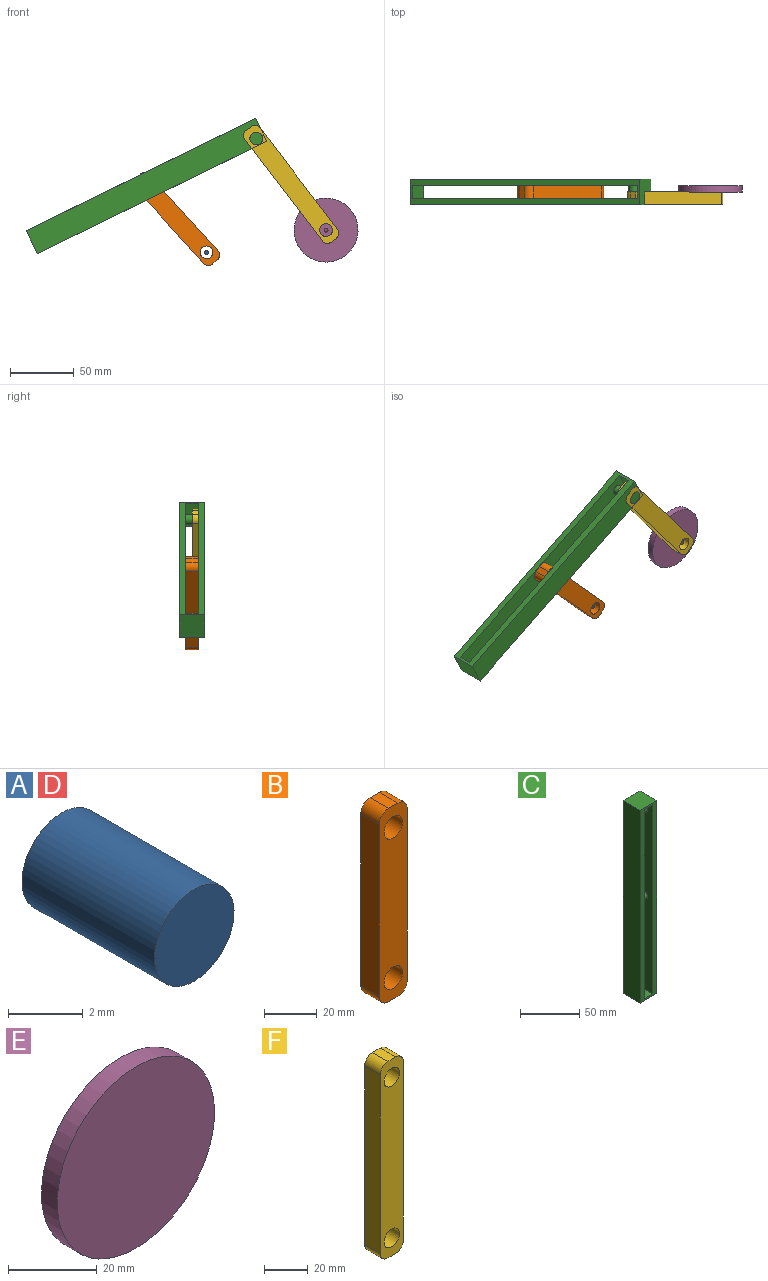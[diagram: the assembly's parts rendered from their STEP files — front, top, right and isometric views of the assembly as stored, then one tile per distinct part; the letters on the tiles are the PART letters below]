
ASSEMBLY  parts=6 mates=5
PART A: 3 faces, bbox 3x5x3 mm
  f0: cylinder r=1.5mm len=5mm, axis (0,1,0), area 47.1mm2, adj f1,f2
  f1: plane 3x3mm, normal (0,-1,0), area 7.1mm2, adj f0
  f2: plane 3x3mm, normal (0,1,0), area 7.1mm2, adj f0
PART B: 12 faces, bbox 15x10x90 mm
  f0: plane 80x10mm, normal (1,0,0), area 800mm2, adj f1,f9,f10,f11
  f1: cylinder r=5mm len=10mm, axis (0,1,0), area 78.5mm2, adj f0,f2,f10,f11
  f2: plane 10x5mm, normal (0,0,1), area 50mm2, adj f1,f3,f10,f11
  f3: cylinder r=5mm len=10mm, axis (0,1,0), area 78.5mm2, adj f2,f4,f10,f11
  f4: plane 80x10mm, normal (-1,0,0), area 800mm2, adj f3,f5,f10,f11
  f5: cylinder r=5mm len=10mm, axis (0,1,0), area 78.5mm2, adj f4,f6,f10,f11
  f6: plane 10x5mm, normal (0,0,-1), area 50mm2, adj f5,f9,f10,f11
  f7: cylinder r=5mm len=10mm, axis (0,1,0), area 314.2mm2, adj f10,f11
  f8: cylinder r=5mm len=10mm, axis (0,1,0), area 314.2mm2, adj f10,f11
  f9: cylinder r=5mm len=10mm, axis (0,1,0), area 78.5mm2, adj f0,f6,f10,f11
  f10: plane 90x15mm, normal (0,-1,0), area 1171.5mm2, adj f0,f1,f2,f3,f4,f5,f6,f7
  f11: plane 90x15mm, normal (0,1,0), area 1171.5mm2, adj f0,f1,f2,f3,f4,f5,f6,f7
PART C: 12 faces, bbox 20x20x200 mm
  f0: plane 200x20mm, normal (0,-1,0), area 2040mm2, adj f2,f3,f4,f5,f6,f7,f8,f9
  f1: plane 200x20mm, normal (0,1,0), area 2040mm2, adj f2,f3,f4,f5,f6,f7,f8,f9
  f2: plane 200x20mm, normal (1,0,0), area 4000mm2, adj f0,f1,f3,f5
  f3: plane 20x20mm, normal (0,0,1), area 400mm2, adj f0,f1,f2,f4
  f4: plane 200x20mm, normal (-1,0,0), area 4000mm2, adj f0,f1,f3,f5
  f5: plane 20x20mm, normal (0,0,-1), area 400mm2, adj f0,f1,f2,f4
  f6: plane 20x10mm, normal (0,0,1), area 200mm2, adj f0,f1,f7,f9
  f7: plane 196x20mm, normal (-1,0,0), area 3819.5mm2, adj f0,f1,f6,f8,f10,f11
  f8: plane 20x10mm, normal (0,0,-1), area 200mm2, adj f0,f1,f7,f9
  f9: plane 196x20mm, normal (1,0,0), area 3819.5mm2, adj f0,f1,f6,f8,f10,f11
  f10: cylinder r=4mm len=10mm, axis (-1,0,0), area 251.3mm2, adj f7,f9
  f11: cylinder r=4mm len=10mm, axis (-1,0,0), area 251.3mm2, adj f7,f9
PART D: same geometry as A
PART E: 3 faces, bbox 50x5x50 mm
  f0: cylinder r=25mm len=50mm, axis (0,1,0), area 785.4mm2, adj f1,f2
  f1: plane 50x50mm, normal (0,-1,0), area 1963.5mm2, adj f0
  f2: plane 50x50mm, normal (0,1,0), area 1963.5mm2, adj f0
PART F: 12 faces, bbox 15x10x110 mm
  f0: plane 100x10mm, normal (1,0,0), area 1000mm2, adj f1,f9,f10,f11
  f1: cylinder r=5mm len=10mm, axis (0,1,0), area 78.5mm2, adj f0,f2,f10,f11
  f2: plane 10x5mm, normal (0,0,1), area 50mm2, adj f1,f3,f10,f11
  f3: cylinder r=5mm len=10mm, axis (0,1,0), area 78.5mm2, adj f2,f4,f10,f11
  f4: plane 100x10mm, normal (-1,0,0), area 1000mm2, adj f3,f5,f10,f11
  f5: cylinder r=5mm len=10mm, axis (0,1,0), area 78.5mm2, adj f4,f6,f10,f11
  f6: plane 10x5mm, normal (0,0,-1), area 50mm2, adj f5,f9,f10,f11
  f7: cylinder r=5mm len=10mm, axis (0,1,0), area 314.2mm2, adj f10,f11
  f8: cylinder r=5mm len=10mm, axis (0,1,0), area 314.2mm2, adj f10,f11
  f9: cylinder r=5mm len=10mm, axis (0,1,0), area 78.5mm2, adj f0,f6,f10,f11
  f10: plane 110x15mm, normal (0,-1,0), area 1471.5mm2, adj f0,f1,f2,f3,f4,f5,f6,f7
  f11: plane 110x15mm, normal (0,1,0), area 1471.5mm2, adj f0,f1,f2,f3,f4,f5,f6,f7
PLACE A t=(25.08,14.46,-57.14)mm fixed
PLACE B rot(axis=(0,-1,0),42.1deg) t=(1.61,16.96,-31.18)mm
PLACE C rot(axis=(-0.47,0.47,-0.75),106.3deg) t=(-17.47,11.96,-14.2)mm
PLACE D t=(118.6,9.46,-39.73)mm fixed
PLACE E rot(axis=(0,-1,0),37.3deg) t=(118.6,14.46,-39.73)mm
PLACE F rot(axis=(0,-1,0),37.3deg) t=(91.31,11.96,-3.95)mm
MATE fastened F.f11 <-> E.f1  axis (0,1,0) through (91.31,11.96,-3.95)mm
MATE revolute B.f7 <-> C.f10  axis (0,1,0) through (-21.86,11.96,-5.22)mm
MATE revolute A.f0 <-> B.f8  axis (0,1,0) through (25.08,11.96,-57.14)mm
MATE revolute F.f3 <-> C.f11  axis (0,1,0) through (59,11.96,34.29)mm
MATE revolute F.f8 <-> D.f0  axis (0,1,0) through (118.6,6.96,-39.73)mm
